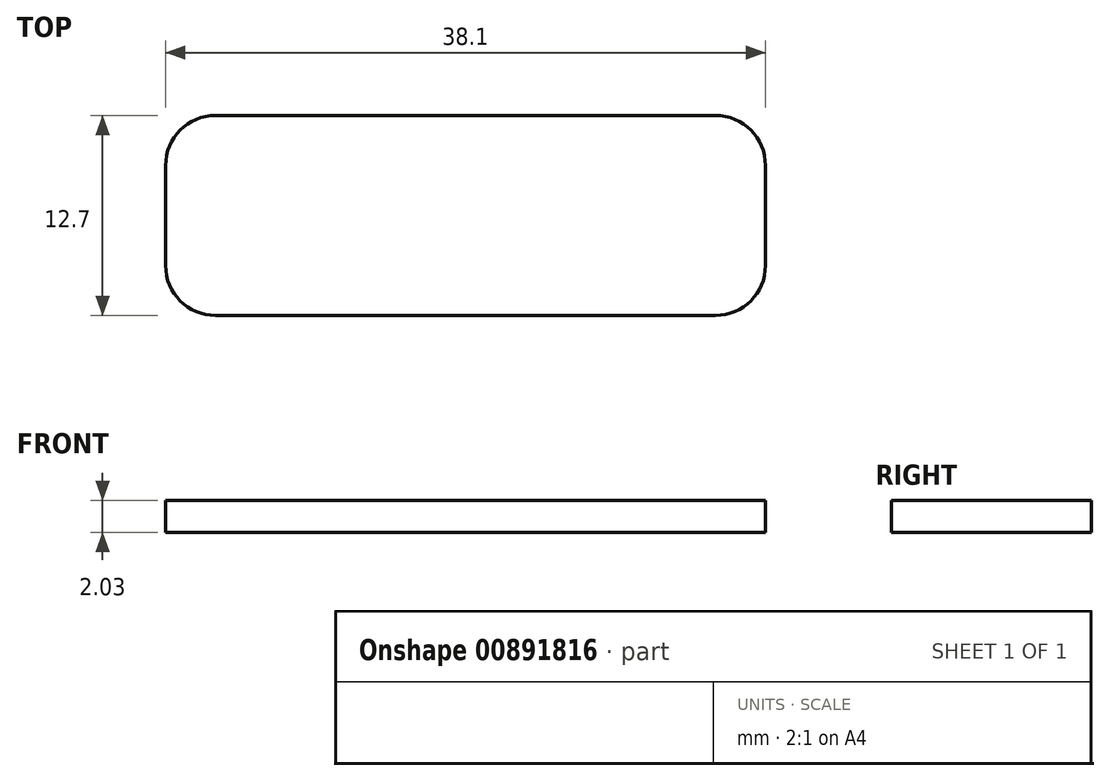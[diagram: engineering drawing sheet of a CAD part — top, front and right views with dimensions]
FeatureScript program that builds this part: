
annotation { "Feature Type Name" : "Feature", "Feature Type Description" : "" }
export const myFeature = defineFeature(function(context is Context, id is Id, definition is map)
    precondition{}
    {
        {
            var Q0;
            Q0=qCreatedBy(makeId("Top.planeOp"),FACE);
            var sketch = newSketch(context, id + "F0", { "sketchPlane" : qUnion([Q0])});
            skLineSegment(sketch, "E0.bottom", {"start": v(-15.88, 6.35) * mm, "end": v(15.88, 6.35) * mm});
            skLineSegment(sketch, "E0.top", {"start": v(-15.88, -6.35) * mm, "end": v(15.88, -6.35) * mm});
            skLineSegment(sketch, "E0.left", {"start": v(-19.05, 3.18) * mm, "end": v(-19.05, -3.17) * mm});
            skLineSegment(sketch, "E0.right", {"start": v(19.05, 3.18) * mm, "end": v(19.05, -3.18) * mm});
            skPoint(sketch, "E0.middle", {"position": v(0, 0) * mm});
            skPoint(sketch, "E1.visualSharp", {"position": v(-19.05, -6.35) * mm});
            skArc(sketch, "E1.filletArc", {"start": v(-19.05, -3.18) * mm, "mid": v(-18.12, -5.42) * mm, "end": v(-15.88, -6.35) * mm});
            skPoint(sketch, "E2.visualSharp", {"position": v(19.05, -6.35) * mm});
            skArc(sketch, "E2.filletArc", {"start": v(15.88, -6.35) * mm, "mid": v(18.12, -5.42) * mm, "end": v(19.05, -3.18) * mm});
            skPoint(sketch, "E3.visualSharp", {"position": v(19.05, 6.35) * mm});
            skArc(sketch, "E3.filletArc", {"start": v(19.05, 3.18) * mm, "mid": v(18.12, 5.42) * mm, "end": v(15.88, 6.35) * mm});
            skPoint(sketch, "E4.visualSharp", {"position": v(-19.05, 6.35) * mm});
            skArc(sketch, "E4.filletArc", {"start": v(-15.88, 6.35) * mm, "mid": v(-18.12, 5.42) * mm, "end": v(-19.05, 3.18) * mm});
            skSolve(sketch);
        }
        {
            var Q0;
            Q0 = qSketchRegion(id + "F0", true);
            extrude(context, id + "F1", {"entities" : qUnion([Q0]), "depth" : 2.03 * mm, "offsetDistance" : 25.4 * mm});
        }
    });
